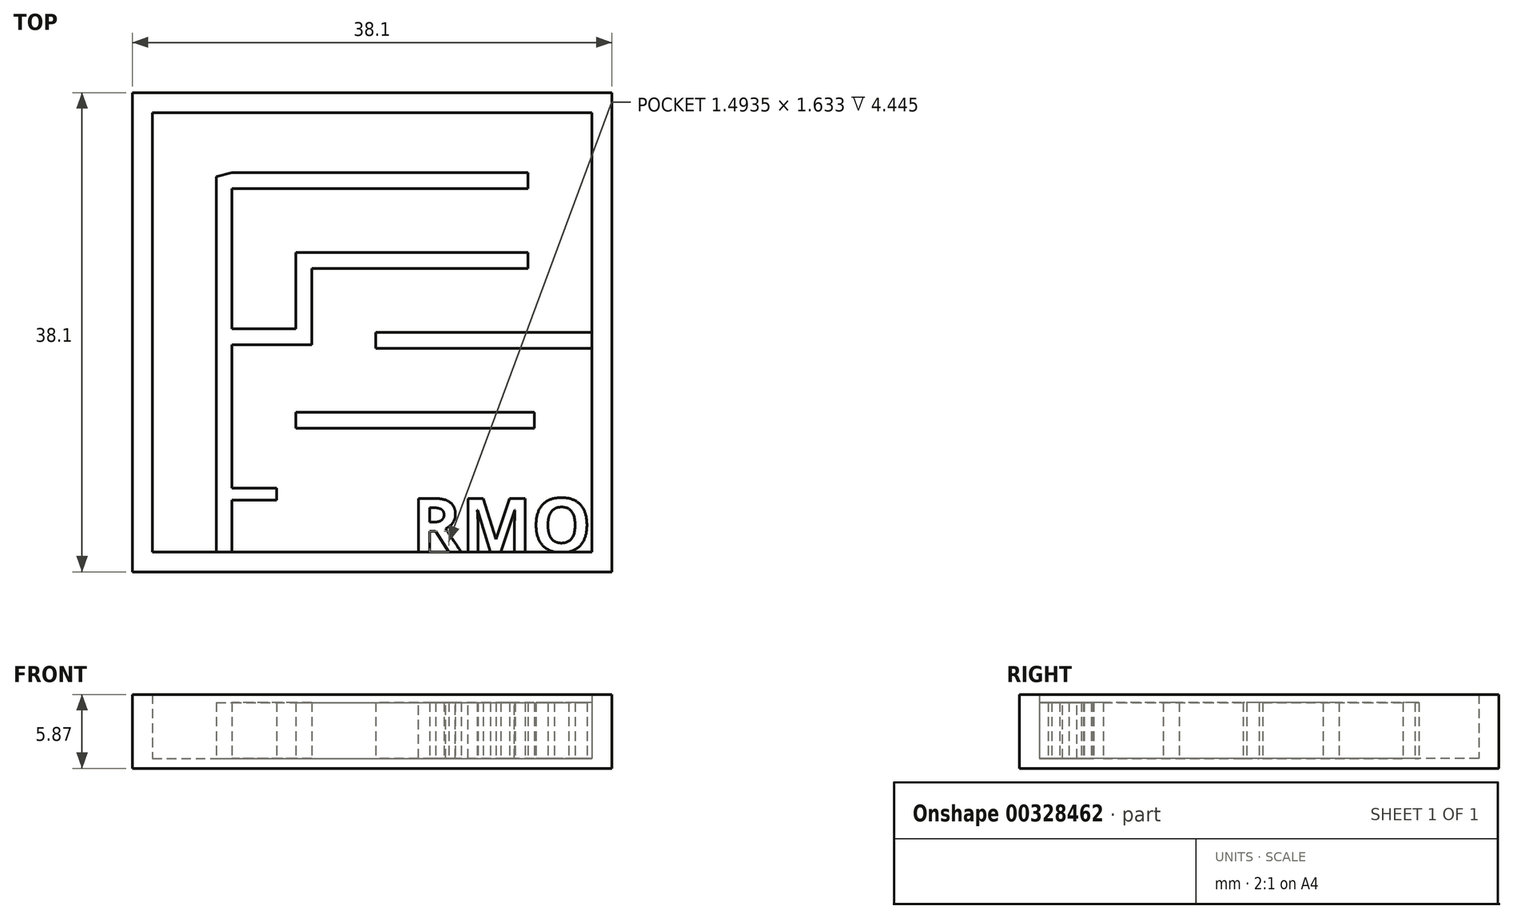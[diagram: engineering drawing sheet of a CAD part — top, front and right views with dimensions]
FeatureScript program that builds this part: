
annotation { "Feature Type Name" : "Feature", "Feature Type Description" : "" }
export const myFeature = defineFeature(function(context is Context, id is Id, definition is map)
    precondition{}
    {
        {
            var Q0;
            Q0=qCreatedBy(makeId("Top.planeOp"),FACE);
            var sketch = newSketch(context, id + "F0", { "sketchPlane" : qUnion([Q0])});
            skLineSegment(sketch, "E0.bottom", {"start": v(-21.25, 16.47) * mm, "end": v(16.85, 16.47) * mm});
            skLineSegment(sketch, "E0.top", {"start": v(-21.25, -21.63) * mm, "end": v(16.85, -21.63) * mm});
            skLineSegment(sketch, "E0.left", {"start": v(-21.25, 16.47) * mm, "end": v(-21.25, -21.63) * mm});
            skLineSegment(sketch, "E0.right", {"start": v(16.85, 16.47) * mm, "end": v(16.85, -21.63) * mm});
            skSolve(sketch);
        }
        {
            var Q0;
            Q0=makeQuery(id+"F0.imprint","IMPRINT",FACE,{"disambiguationData":[TD([[makeQuery(id+"F0.imprint","IMPRINT",EDGE,{"derivedFrom":sQuery(id+"F0.wireOp",EDGE,"E0.bottom")}),-1.0]])]});
            extrude(context, id + "F1", {"entities" : qUnion([Q0]), "depth" : 0.8 * mm});
        }
        {
            var Q0;
            Q0=makeQuery(id+"F1.opExtrude","CAP_FACE",FACE,{"disambiguationData":[OSD([sQuery(id+"F0.wireOp",EDGE,"E0.bottom"),sQuery(id+"F0.wireOp",EDGE,"E0.top"),sQuery(id+"F0.wireOp",EDGE,"E0.left"),sQuery(id+"F0.wireOp",EDGE,"E0.right")])],"isStart":false});
            var sketch = newSketch(context, id + "F2", { "sketchPlane" : qUnion([Q0])});
            skLineSegment(sketch, "E1.0", {"start": v(-19.66, 14.88) * mm, "end": v(15.26, 14.88) * mm});
            skLineSegment(sketch, "E1.1", {"start": v(-19.66, 14.88) * mm, "end": v(-19.66, -20.04) * mm});
            skLineSegment(sketch, "E1.2", {"start": v(-19.66, -20.04) * mm, "end": v(15.26, -20.04) * mm});
            skLineSegment(sketch, "E1.3", {"start": v(15.26, 14.88) * mm, "end": v(15.26, -20.04) * mm});
            skSolve(sketch);
        }
        {
            var Q0;
            Q0=makeQuery(id+"F2.imprint","IMPRINT",FACE,{"disambiguationData":[TD([[makeQuery(id+"F2.imprint","IMPRINT",EDGE,{"derivedFrom":sQuery(id+"F2.wireOp",EDGE,"E1.0")}),1.0]])]});
            extrude(context, id + "F3", {"entities" : qUnion([Q0]), "operationType" : NewBodyOperationType.ADD, "depth" : 5.08 * mm});
        }
        {
            var Q0;
            Q0=makeQuery(id+"F1.opExtrude","CAP_FACE",FACE,{"disambiguationData":[OSD([sQuery(id+"F0.wireOp",EDGE,"E0.bottom"),sQuery(id+"F0.wireOp",EDGE,"E0.top"),sQuery(id+"F0.wireOp",EDGE,"E0.left"),sQuery(id+"F0.wireOp",EDGE,"E0.right")])],"isStart":false});
            var sketch = newSketch(context, id + "F4", { "sketchPlane" : qUnion([Q0])});
            skLineSegment(sketch, "E2", {"start": v(-13.35, -20.04) * mm, "end": v(-13.35, 10.12) * mm});
            skLineSegment(sketch, "E3", {"start": v(-14.58, 9.8) * mm, "end": v(-14.58, -20.04) * mm});
            skLineSegment(sketch, "E4", {"start": v(-14.58, 9.8) * mm, "end": v(-13.35, 10.12) * mm});
            skText(sketch, "E5", { "text": "RMO", "fontName": "OpenSans-Bold.ttf"});
            skLineSegment(sketch, "E6.bottom", {"start": v(-13.35, 10.12) * mm, "end": v(10.18, 10.12) * mm});
            skLineSegment(sketch, "E6.top", {"start": v(-13.35, 8.85) * mm, "end": v(10.18, 8.85) * mm});
            skLineSegment(sketch, "E6.left", {"start": v(-13.35, 10.12) * mm, "end": v(-13.35, 8.85) * mm});
            skLineSegment(sketch, "E6.right", {"start": v(10.18, 10.12) * mm, "end": v(10.18, 8.85) * mm});
            skLineSegment(sketch, "E7.bottom", {"start": v(-8.27, 3.77) * mm, "end": v(10.18, 3.77) * mm});
            skLineSegment(sketch, "E7.top", {"start": v(-8.27, 2.5) * mm, "end": v(10.18, 2.5) * mm});
            skLineSegment(sketch, "E7.left", {"start": v(-8.27, 3.77) * mm, "end": v(-8.27, 2.5) * mm});
            skLineSegment(sketch, "E7.right", {"start": v(10.18, 3.77) * mm, "end": v(10.18, 2.5) * mm});
            skLineSegment(sketch, "E8.bottom", {"start": v(-8.27, 2.5) * mm, "end": v(-7, 2.5) * mm});
            skLineSegment(sketch, "E8.top", {"start": v(-8.27, -3.56) * mm, "end": v(-7, -3.56) * mm});
            skLineSegment(sketch, "E8.left", {"start": v(-8.27, 2.5) * mm, "end": v(-8.27, -3.56) * mm});
            skLineSegment(sketch, "E8.right", {"start": v(-7, 2.5) * mm, "end": v(-7, -3.56) * mm});
            skLineSegment(sketch, "E9.bottom", {"start": v(-8.27, -3.56) * mm, "end": v(-13.35, -3.56) * mm});
            skLineSegment(sketch, "E9.top", {"start": v(-8.27, -2.3) * mm, "end": v(-13.35, -2.3) * mm});
            skLineSegment(sketch, "E9.left", {"start": v(-8.27, -3.56) * mm, "end": v(-8.27, -2.3) * mm});
            skLineSegment(sketch, "E9.right", {"start": v(-13.35, -3.56) * mm, "end": v(-13.35, -2.3) * mm});
            skPoint(sketch, "E10.oppositeSnap0", {"position": v(15.26, -2.58) * mm});
            skLineSegment(sketch, "E10.bottom", {"start": v(15.26, -3.85) * mm, "end": v(-1.92, -3.85) * mm});
            skLineSegment(sketch, "E10.top", {"start": v(15.26, -2.58) * mm, "end": v(-1.92, -2.58) * mm});
            skLineSegment(sketch, "E10.left", {"start": v(15.26, -3.85) * mm, "end": v(15.26, -2.58) * mm});
            skLineSegment(sketch, "E10.right", {"start": v(-1.92, -3.85) * mm, "end": v(-1.92, -2.58) * mm});
            skLineSegment(sketch, "E11.bottom", {"start": v(-8.27, -8.93) * mm, "end": v(10.7, -8.93) * mm});
            skLineSegment(sketch, "E11.top", {"start": v(-8.27, -10.2) * mm, "end": v(10.7, -10.2) * mm});
            skLineSegment(sketch, "E11.left", {"start": v(-8.27, -8.93) * mm, "end": v(-8.27, -10.2) * mm});
            skLineSegment(sketch, "E11.right", {"start": v(10.7, -8.93) * mm, "end": v(10.7, -10.2) * mm});
            skLineSegment(sketch, "E12.bottom", {"start": v(-13.35, -15.92) * mm, "end": v(-9.79, -15.92) * mm});
            skLineSegment(sketch, "E12.top", {"start": v(-13.35, -14.96) * mm, "end": v(-9.79, -14.96) * mm});
            skLineSegment(sketch, "E12.left", {"start": v(-13.35, -14.96) * mm, "end": v(-13.35, -15.92) * mm});
            skLineSegment(sketch, "E12.right", {"start": v(-9.79, -14.96) * mm, "end": v(-9.79, -15.92) * mm});
            skLineSegment(sketch, "E13.left", {"start": v(15.26, -15.92) * mm, "end": v(15.26, -17.19) * mm});
            const initialGuessF4  = {"E5": [0.00095, -0.02004, 1, 0, 0.00428]};
            skSetInitialGuess(sketch, initialGuessF4);
            skSolve(sketch);
        }
        {
            var Q0;
            Q0 = qSketchRegion(id + "F4", true);
            var Q1;
            {var subQ0=sQuery(id+"F4.wireOp",EDGE,"E3");Q1=makeQuery(id+"F4.imprint","IMPRINT",FACE,{"disambiguationData":[TD([[makeQuery(id+"F4.imprint","IMPRINT",EDGE,{"derivedFrom":subQ0}),1.0]])]});}
            extrude(context, id + "F5", {"entities" : qUnion([Q0, Q1]), "operationType" : NewBodyOperationType.ADD, "depth" : 4.44 * mm});
        }
        {
            var Q0;
            Q0=makeQuery(id+"F5.boolean.opBoolean","SPLIT",FACE,{"disambiguationData":[TD([makeQuery(id+"F3.opExtrude","SWEPT_FACE",FACE,{"disambiguationData":[OSD([sQuery(id+"F2.wireOp",EDGE,"E1.0")])]})])],"derivedFrom":makeQuery(id+"F1.opExtrude","CAP_FACE",FACE,{"disambiguationData":[OSD([sQuery(id+"F0.wireOp",EDGE,"E0.bottom"),sQuery(id+"F0.wireOp",EDGE,"E0.top"),sQuery(id+"F0.wireOp",EDGE,"E0.left"),sQuery(id+"F0.wireOp",EDGE,"E0.right")])],"isStart":false})});
            var sketch = newSketch(context, id + "F6", { "sketchPlane" : qUnion([Q0])});
            skCircle(sketch, "E14", {"center": v(-17.12, -16.23) * mm, "radius": 1.27 * mm});
            skPoint(sketch, "E14.centerSnap0", {"position": v(-17.12, -20.04) * mm});
            skCircle(sketch, "E15", {"center": v(-7.22, -17.98) * mm, "radius": 1.27 * mm});
            skPoint(sketch, "E15.centerSnap0", {"position": v(-13.35, -17.98) * mm});
            skSolve(sketch);
        }
        {
            var Q0;
            Q0=sQuery(id+"F6.wireOp",EDGE,"E15");
            var Q1;
            Q1=sQuery(id+"F6.wireOp",EDGE,"E14");
            extrude(context, id + "F7", {"bodyType" : ToolBodyType.SURFACE, "surfaceEntities" : qUnion([Q0, Q1]), "depth" : 0.4 * mm});
        }
    });
